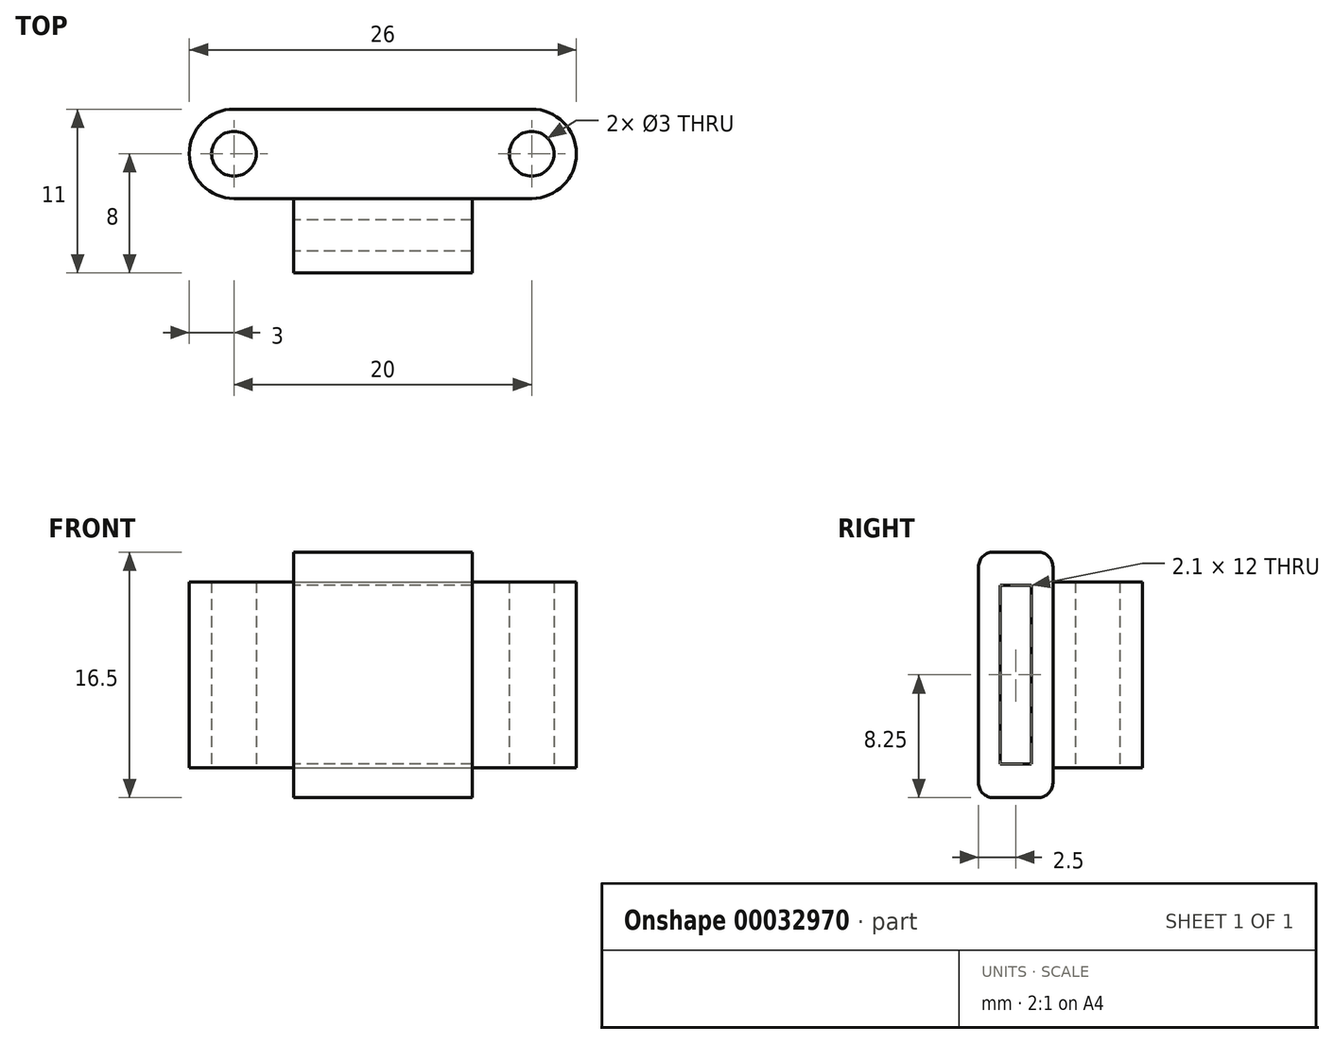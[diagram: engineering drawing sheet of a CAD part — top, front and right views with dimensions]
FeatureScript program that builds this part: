
annotation { "Feature Type Name" : "Feature", "Feature Type Description" : "" }
export const myFeature = defineFeature(function(context is Context, id is Id, definition is map)
    precondition{}
    {
        {
            var Q0;
            Q0=qCreatedBy(makeId("Front.planeOp"),FACE);
            var sketch = newSketch(context, id + "F0", { "sketchPlane" : qUnion([Q0])});
            skLineSegment(sketch, "E0.rect.bottom", {"start": v(6, -8.25) * mm, "end": v(-6, -8.25) * mm});
            skLineSegment(sketch, "E0.rect.top", {"start": v(6, 8.25) * mm, "end": v(-6, 8.25) * mm});
            skLineSegment(sketch, "E0.rect.left", {"start": v(6, -8.25) * mm, "end": v(6, 8.25) * mm});
            skLineSegment(sketch, "E0.rect.right", {"start": v(-6, -8.25) * mm, "end": v(-6, 8.25) * mm});
            skPoint(sketch, "E0.rect.middle", {"position": v(0, 0) * mm});
            skSolve(sketch);
        }
        {
            var Q0;
            Q0 = qSketchRegion(id + "F0", true);
            extrude(context, id + "F1", {"entities" : qUnion([Q0]), "depth" : 5 * mm});
        }
        {
            var Q0;
            Q0=qCreatedBy(makeId("Top.planeOp"),FACE);
            var sketch = newSketch(context, id + "F2", { "sketchPlane" : qUnion([Q0])});
            skLineSegment(sketch, "E1", {"start": v(0, 3) * mm, "end": v(10, 3) * mm, "construction": true});
            skCircle(sketch, "E2", {"center": v(10, 3) * mm, "radius": 1.5 * mm});
            skArc(sketch, "E3", {"start": v(10, 0) * mm, "mid": v(13, 3) * mm, "end": v(10, 6) * mm});
            skCircle(sketch, "E4.MirrorC", {"center": v(-10, 3) * mm, "radius": 1.5 * mm});
            skArc(sketch, "E5.MirrorC", {"start": v(-10, 0) * mm, "mid": v(-13, 3) * mm, "end": v(-10, 6) * mm});
            skLineSegment(sketch, "E6", {"start": v(-10, 6) * mm, "end": v(10, 6) * mm});
            skLineSegment(sketch, "E7", {"start": v(-10, 0) * mm, "end": v(10, 0) * mm});
            skSolve(sketch);
        }
        {
            var Q0;
            Q0 = qSketchRegion(id + "F2", true);
            extrude(context, id + "F3", {"entities" : qUnion([Q0]), "operationType" : NewBodyOperationType.ADD, "depth" : 12.5 * mm, "symmetric" : true});
        }
        {
            var Q0;
            Q0=makeQuery(id+"F1.opExtrude","SWEPT_FACE",FACE,{"disambiguationData":[OSD([sQuery(id+"F0.wireOp",EDGE,"E0.rect.right")])]});
            var sketch = newSketch(context, id + "F4", { "sketchPlane" : qUnion([Q0])});
            skLineSegment(sketch, "E8", {"start": v(2.5, 8.25) * mm, "end": v(2.5, -8.25) * mm, "construction": true});
            skLineSegment(sketch, "E9.rect.bottom", {"start": v(3.55, -6) * mm, "end": v(1.45, -6) * mm});
            skLineSegment(sketch, "E9.rect.top", {"start": v(3.55, 6) * mm, "end": v(1.45, 6) * mm});
            skLineSegment(sketch, "E9.rect.left", {"start": v(3.55, -6) * mm, "end": v(3.55, 6) * mm});
            skLineSegment(sketch, "E9.rect.right", {"start": v(1.45, -6) * mm, "end": v(1.45, 6) * mm});
            skPoint(sketch, "E9.rect.middle", {"position": v(2.5, 0) * mm});
            skSolve(sketch);
        }
        {
            var Q0;
            Q0 = qSketchRegion(id + "F4", true);
            extrude(context, id + "F5", {"entities" : qUnion([Q0]), "operationType" : NewBodyOperationType.REMOVE, "endBound" : BoundingType.UP_TO_NEXT, "oppositeDirection" : true, "depth" : 25 * mm});
        }
        {
            var Q0;
            Q0=makeQuery(id+"F1.opExtrude","CAP_EDGE",EDGE,{"disambiguationData":[OSD([sQuery(id+"F0.wireOp",EDGE,"E0.rect.top")])],"isStart":false});
            var Q1;
            Q1=makeQuery(id+"F1.opExtrude","CAP_EDGE",EDGE,{"disambiguationData":[OSD([sQuery(id+"F0.wireOp",EDGE,"E0.rect.top")])],"isStart":true});
            var Q2;
            Q2=makeQuery(id+"F1.opExtrude","CAP_EDGE",EDGE,{"disambiguationData":[OSD([sQuery(id+"F0.wireOp",EDGE,"E0.rect.bottom")])],"isStart":true});
            var Q3;
            Q3=makeQuery(id+"F1.opExtrude","CAP_EDGE",EDGE,{"disambiguationData":[OSD([sQuery(id+"F0.wireOp",EDGE,"E0.rect.bottom")])],"isStart":false});
            fillet(context, id + "F6", {"entities" : qUnion([Q0, Q1, Q2, Q3]), "radius" : 1 * mm, "tangentPropagation" : true, "allowEdgeOverflow" : false});
        }
    });
